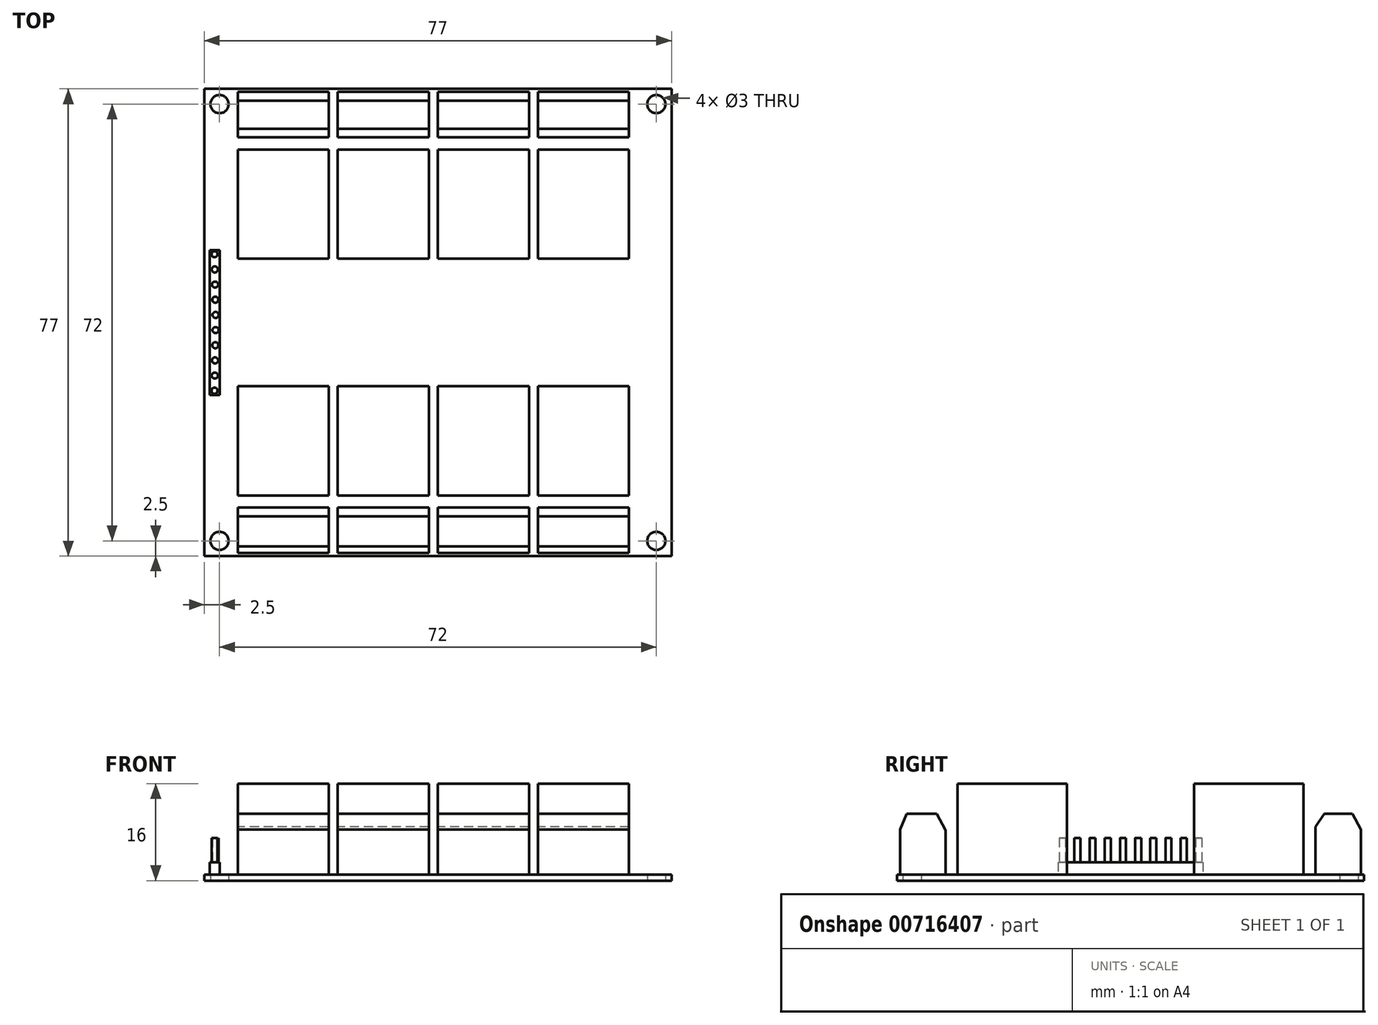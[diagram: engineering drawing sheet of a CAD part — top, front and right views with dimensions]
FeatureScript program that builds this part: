
annotation { "Feature Type Name" : "Feature", "Feature Type Description" : "" }
export const myFeature = defineFeature(function(context is Context, id is Id, definition is map)
    precondition{}
    {
        {
            var Q0;
            Q0=qCreatedBy(makeId("Top.planeOp"),FACE);
            var sketch = newSketch(context, id + "F0", { "sketchPlane" : qUnion([Q0])});
            skLineSegment(sketch, "E0.bottom", {"start": v(0, 0) * mm, "end": v(77, 0) * mm});
            skLineSegment(sketch, "E0.top", {"start": v(0, 77) * mm, "end": v(77, 77) * mm});
            skLineSegment(sketch, "E0.left", {"start": v(0, 0) * mm, "end": v(0, 77) * mm});
            skLineSegment(sketch, "E0.right", {"start": v(77, 0) * mm, "end": v(77, 77) * mm});
            skLineSegment(sketch, "E1", {"start": v(38.5, 77) * mm, "end": v(38.5, 0) * mm, "construction": true});
            skLineSegment(sketch, "E2", {"start": v(77, 38.5) * mm, "end": v(0, 38.5) * mm, "construction": true});
            skCircle(sketch, "E3", {"center": v(2.5, 2.5) * mm, "radius": 1.5 * mm});
            skCircle(sketch, "E4.MirrorC", {"center": v(74.5, 2.5) * mm, "radius": 1.5 * mm});
            skLineSegment(sketch, "E5.MirrorCS", {"start": v(0, 38.5) * mm, "end": v(77, 38.5) * mm, "construction": true});
            skCircle(sketch, "E6.MirrorC", {"center": v(74.5, 74.5) * mm, "radius": 1.5 * mm});
            skCircle(sketch, "E7.MirrorC", {"center": v(2.5, 74.5) * mm, "radius": 1.5 * mm});
            skSolve(sketch);
        }
        {
            var Q0;
            Q0 = qSketchRegion(id + "F0", true);
            extrude(context, id + "F1", {"entities" : qUnion([Q0]), "depth" : 1 * mm, "offsetDistance" : 25 * mm});
        }
        {
            var Q0;
            Q0=makeQuery(id+"F1.opExtrude","CAP_FACE",FACE,{"disambiguationData":[OSD([sQuery(id+"F0.wireOp",EDGE,"E0.bottom"),sQuery(id+"F0.wireOp",EDGE,"E0.top"),sQuery(id+"F0.wireOp",EDGE,"E0.left"),sQuery(id+"F0.wireOp",EDGE,"E0.right"),sQuery(id+"F0.wireOp",EDGE,"E3"),sQuery(id+"F0.wireOp",EDGE,"E4.MirrorC"),sQuery(id+"F0.wireOp",EDGE,"E6.MirrorC"),sQuery(id+"F0.wireOp",EDGE,"E7.MirrorC")])],"isStart":false});
            var sketch = newSketch(context, id + "F2", { "sketchPlane" : qUnion([Q0])});
            skLineSegment(sketch, "E8.bottom", {"start": v(5.5, 67) * mm, "end": v(20.5, 67) * mm});
            skLineSegment(sketch, "E8.top", {"start": v(5.5, 49) * mm, "end": v(20.5, 49) * mm});
            skLineSegment(sketch, "E8.left", {"start": v(5.5, 67) * mm, "end": v(5.5, 49) * mm});
            skLineSegment(sketch, "E8.right", {"start": v(20.5, 67) * mm, "end": v(20.5, 49) * mm});
            skLineSegment(sketch, "E9.1.0.0", {"start": v(37, 67) * mm, "end": v(37, 49) * mm});
            skLineSegment(sketch, "E9.1.0.1", {"start": v(22, 67) * mm, "end": v(22, 49) * mm});
            skLineSegment(sketch, "E9.1.0.2", {"start": v(22, 49) * mm, "end": v(37, 49) * mm});
            skLineSegment(sketch, "E9.1.0.3", {"start": v(22, 67) * mm, "end": v(37, 67) * mm});
            skLineSegment(sketch, "E9.2.0.0", {"start": v(53.5, 67) * mm, "end": v(53.5, 49) * mm});
            skLineSegment(sketch, "E9.2.0.1", {"start": v(38.5, 67) * mm, "end": v(38.5, 49) * mm});
            skLineSegment(sketch, "E9.2.0.2", {"start": v(38.5, 49) * mm, "end": v(53.5, 49) * mm});
            skLineSegment(sketch, "E9.2.0.3", {"start": v(38.5, 67) * mm, "end": v(53.5, 67) * mm});
            skLineSegment(sketch, "E9.3.0.0", {"start": v(70, 67) * mm, "end": v(70, 49) * mm});
            skLineSegment(sketch, "E9.3.0.1", {"start": v(55, 67) * mm, "end": v(55, 49) * mm});
            skLineSegment(sketch, "E9.3.0.2", {"start": v(55, 49) * mm, "end": v(70, 49) * mm});
            skLineSegment(sketch, "E9.3.0.3", {"start": v(55, 67) * mm, "end": v(70, 67) * mm});
            skLineSegment(sketch, "E9.direction1", {"start": v(5.5, 49) * mm, "end": v(22, 49) * mm, "construction": true});
            skLineSegment(sketch, "E10", {"start": v(0, 38.5) * mm, "end": v(77, 38.5) * mm, "construction": true});
            skLineSegment(sketch, "E11.MirrorCS", {"start": v(5.5, 28) * mm, "end": v(20.5, 28) * mm});
            skLineSegment(sketch, "E12.MirrorCS", {"start": v(22, 10) * mm, "end": v(37, 10) * mm});
            skLineSegment(sketch, "E13.MirrorCS", {"start": v(53.5, 10) * mm, "end": v(53.5, 28) * mm});
            skLineSegment(sketch, "E14.MirrorCS", {"start": v(22, 28) * mm, "end": v(37, 28) * mm});
            skLineSegment(sketch, "E15.MirrorCS", {"start": v(22, 10) * mm, "end": v(22, 28) * mm});
            skLineSegment(sketch, "E16.MirrorCS", {"start": v(37, 10) * mm, "end": v(37, 28) * mm});
            skLineSegment(sketch, "E17.MirrorCS", {"start": v(20.5, 10) * mm, "end": v(20.5, 28) * mm});
            skLineSegment(sketch, "E18.MirrorCS", {"start": v(5.5, 10) * mm, "end": v(5.5, 28) * mm});
            skLineSegment(sketch, "E19.MirrorCS", {"start": v(5.5, 10) * mm, "end": v(20.5, 10) * mm});
            skLineSegment(sketch, "E20.MirrorCS", {"start": v(55, 10) * mm, "end": v(70, 10) * mm});
            skLineSegment(sketch, "E21.MirrorCS", {"start": v(55, 28) * mm, "end": v(70, 28) * mm});
            skLineSegment(sketch, "E22.MirrorCS", {"start": v(55, 10) * mm, "end": v(55, 28) * mm});
            skLineSegment(sketch, "E23.MirrorCS", {"start": v(5.5, 28) * mm, "end": v(22, 28) * mm, "construction": true});
            skLineSegment(sketch, "E24.MirrorCS", {"start": v(38.5, 10) * mm, "end": v(38.5, 28) * mm});
            skLineSegment(sketch, "E25.MirrorCS", {"start": v(38.5, 28) * mm, "end": v(53.5, 28) * mm});
            skLineSegment(sketch, "E26.MirrorCS", {"start": v(38.5, 10) * mm, "end": v(53.5, 10) * mm});
            skLineSegment(sketch, "E27.MirrorCS", {"start": v(70, 10) * mm, "end": v(70, 28) * mm});
            skSolve(sketch);
        }
        {
            var Q0;
            Q0 = qSketchRegion(id + "F2", true);
            extrude(context, id + "F3", {"entities" : qUnion([Q0]), "operationType" : NewBodyOperationType.ADD, "depth" : 15 * mm, "offsetDistance" : 25 * mm});
        }
        {
            var Q0;
            Q0=makeQuery(id+"F1.opExtrude","CAP_FACE",FACE,{"disambiguationData":[OSD([sQuery(id+"F0.wireOp",EDGE,"E0.bottom"),sQuery(id+"F0.wireOp",EDGE,"E0.top"),sQuery(id+"F0.wireOp",EDGE,"E0.left"),sQuery(id+"F0.wireOp",EDGE,"E0.right"),sQuery(id+"F0.wireOp",EDGE,"E3"),sQuery(id+"F0.wireOp",EDGE,"E4.MirrorC"),sQuery(id+"F0.wireOp",EDGE,"E6.MirrorC"),sQuery(id+"F0.wireOp",EDGE,"E7.MirrorC")])],"isStart":false});
            var sketch = newSketch(context, id + "F4", { "sketchPlane" : qUnion([Q0])});
            skLineSegment(sketch, "E28.bottom", {"start": v(5.5, 69) * mm, "end": v(20.5, 69) * mm});
            skLineSegment(sketch, "E28.top", {"start": v(5.5, 76.5) * mm, "end": v(20.5, 76.5) * mm});
            skLineSegment(sketch, "E28.left", {"start": v(5.5, 69) * mm, "end": v(5.5, 76.5) * mm});
            skLineSegment(sketch, "E28.right", {"start": v(20.5, 69) * mm, "end": v(20.5, 76.5) * mm});
            skLineSegment(sketch, "E29.1.0.0", {"start": v(37, 69) * mm, "end": v(37, 76.5) * mm});
            skLineSegment(sketch, "E29.1.0.1", {"start": v(22, 69) * mm, "end": v(22, 76.5) * mm});
            skLineSegment(sketch, "E29.1.0.2", {"start": v(22, 76.5) * mm, "end": v(37, 76.5) * mm});
            skLineSegment(sketch, "E29.1.0.3", {"start": v(22, 69) * mm, "end": v(37, 69) * mm});
            skLineSegment(sketch, "E29.2.0.0", {"start": v(53.5, 69) * mm, "end": v(53.5, 76.5) * mm});
            skLineSegment(sketch, "E29.2.0.1", {"start": v(38.5, 69) * mm, "end": v(38.5, 76.5) * mm});
            skLineSegment(sketch, "E29.2.0.2", {"start": v(38.5, 76.5) * mm, "end": v(53.5, 76.5) * mm});
            skLineSegment(sketch, "E29.2.0.3", {"start": v(38.5, 69) * mm, "end": v(53.5, 69) * mm});
            skLineSegment(sketch, "E29.3.0.0", {"start": v(70, 69) * mm, "end": v(70, 76.5) * mm});
            skLineSegment(sketch, "E29.3.0.1", {"start": v(55, 69) * mm, "end": v(55, 76.5) * mm});
            skLineSegment(sketch, "E29.3.0.2", {"start": v(55, 76.5) * mm, "end": v(70, 76.5) * mm});
            skLineSegment(sketch, "E29.3.0.3", {"start": v(55, 69) * mm, "end": v(70, 69) * mm});
            skLineSegment(sketch, "E30", {"start": v(0, 38.5) * mm, "end": v(77, 38.5) * mm, "construction": true});
            skLineSegment(sketch, "E31.MirrorCS", {"start": v(55, 8) * mm, "end": v(55, 0.5) * mm});
            skLineSegment(sketch, "E32.MirrorCS", {"start": v(55, 0.5) * mm, "end": v(70, 0.5) * mm});
            skLineSegment(sketch, "E33.MirrorCS", {"start": v(55, 8) * mm, "end": v(70, 8) * mm});
            skLineSegment(sketch, "E34.MirrorCS", {"start": v(5.5, 8) * mm, "end": v(20.5, 8) * mm});
            skLineSegment(sketch, "E35.MirrorCS", {"start": v(22, 8) * mm, "end": v(22, 0.5) * mm});
            skLineSegment(sketch, "E36.MirrorCS", {"start": v(70, 8) * mm, "end": v(70, 0.5) * mm});
            skLineSegment(sketch, "E37.MirrorCS", {"start": v(5.5, 0.5) * mm, "end": v(20.5, 0.5) * mm});
            skLineSegment(sketch, "E38.MirrorCS", {"start": v(20.5, 8) * mm, "end": v(20.5, 0.5) * mm});
            skLineSegment(sketch, "E39.MirrorCS", {"start": v(37, 8) * mm, "end": v(37, 0.5) * mm});
            skLineSegment(sketch, "E40.MirrorCS", {"start": v(38.5, 8) * mm, "end": v(38.5, 0.5) * mm});
            skLineSegment(sketch, "E41.MirrorCS", {"start": v(5.5, 8) * mm, "end": v(5.5, 0.5) * mm});
            skLineSegment(sketch, "E42.MirrorCS", {"start": v(22, 8) * mm, "end": v(37, 8) * mm});
            skLineSegment(sketch, "E43.MirrorCS", {"start": v(38.5, 8) * mm, "end": v(53.5, 8) * mm});
            skLineSegment(sketch, "E44.MirrorCS", {"start": v(38.5, 0.5) * mm, "end": v(53.5, 0.5) * mm});
            skLineSegment(sketch, "E45.MirrorCS", {"start": v(53.5, 8) * mm, "end": v(53.5, 0.5) * mm});
            skLineSegment(sketch, "E46.MirrorCS", {"start": v(22, 0.5) * mm, "end": v(37, 0.5) * mm});
            skSolve(sketch);
        }
        {
            var Q0;
            Q0 = qSketchRegion(id + "F4", true);
            extrude(context, id + "F5", {"entities" : qUnion([Q0]), "operationType" : NewBodyOperationType.ADD, "depth" : 10 * mm, "offsetDistance" : 25 * mm});
        }
        {
            var Q0;
            Q0=makeQuery(id+"F1.opExtrude","CAP_FACE",FACE,{"disambiguationData":[OSD([sQuery(id+"F0.wireOp",EDGE,"E0.bottom"),sQuery(id+"F0.wireOp",EDGE,"E0.top"),sQuery(id+"F0.wireOp",EDGE,"E0.left"),sQuery(id+"F0.wireOp",EDGE,"E0.right"),sQuery(id+"F0.wireOp",EDGE,"E3"),sQuery(id+"F0.wireOp",EDGE,"E4.MirrorC"),sQuery(id+"F0.wireOp",EDGE,"E6.MirrorC"),sQuery(id+"F0.wireOp",EDGE,"E7.MirrorC")])],"isStart":false});
            var sketch = newSketch(context, id + "F6", { "sketchPlane" : qUnion([Q0])});
            skLineSegment(sketch, "E47", {"start": v(0, 38.5) * mm, "end": v(77, 38.5) * mm, "construction": true});
            skCircle(sketch, "E48", {"center": v(1.86, 39.75) * mm, "radius": 0.5 * mm});
            skCircle(sketch, "E49.1.0.0", {"center": v(1.81, 42.25) * mm, "radius": 0.5 * mm});
            skCircle(sketch, "E49.2.0.0", {"center": v(1.77, 44.75) * mm, "radius": 0.5 * mm});
            skCircle(sketch, "E49.3.0.0", {"center": v(1.73, 47.25) * mm, "radius": 0.5 * mm});
            skCircle(sketch, "E49.4.0.0", {"center": v(1.68, 49.75) * mm, "radius": 0.5 * mm});
            skCircle(sketch, "E50.MirrorC", {"center": v(1.86, 37.25) * mm, "radius": 0.5 * mm});
            skCircle(sketch, "E51.MirrorC", {"center": v(1.77, 32.25) * mm, "radius": 0.5 * mm});
            skCircle(sketch, "E52.MirrorC", {"center": v(1.68, 27.25) * mm, "radius": 0.5 * mm});
            skCircle(sketch, "E53.MirrorC", {"center": v(1.73, 29.75) * mm, "radius": 0.5 * mm});
            skCircle(sketch, "E54.MirrorC", {"center": v(1.81, 34.75) * mm, "radius": 0.5 * mm});
            skSolve(sketch);
        }
        {
            var Q0;
            Q0 = qSketchRegion(id + "F6", true);
            extrude(context, id + "F7", {"entities" : qUnion([Q0]), "operationType" : NewBodyOperationType.ADD, "depth" : 6 * mm, "offsetDistance" : 25 * mm});
        }
        {
            var Q0;
            Q0=makeQuery(id+"F5.opExtrude","SWEPT_FACE",FACE,{"disambiguationData":[OSD([sQuery(id+"F4.wireOp",EDGE,"E28.left")])]});
            var sketch = newSketch(context, id + "F8", { "sketchPlane" : qUnion([Q0])});
            skLineSegment(sketch, "E55", {"start": v(-75.06, 11) * mm, "end": v(-76.5, 8.45) * mm});
            skLineSegment(sketch, "E56", {"start": v(-76.5, 8.45) * mm, "end": v(-76.5, 11) * mm});
            skLineSegment(sketch, "E57", {"start": v(-76.5, 11) * mm, "end": v(-75.06, 11) * mm});
            skLineSegment(sketch, "E58", {"start": v(-69, 11) * mm, "end": v(-70.42, 11) * mm});
            skLineSegment(sketch, "E59", {"start": v(-70.42, 11) * mm, "end": v(-69, 8.88) * mm});
            skLineSegment(sketch, "E60", {"start": v(-69, 8.88) * mm, "end": v(-69, 11) * mm});
            skLineSegment(sketch, "E61", {"start": v(-8.03, 11) * mm, "end": v(-8.03, 8.25) * mm});
            skLineSegment(sketch, "E62", {"start": v(-8.03, 8.25) * mm, "end": v(-6.55, 11) * mm});
            skLineSegment(sketch, "E63", {"start": v(-6.55, 11) * mm, "end": v(-8.03, 11) * mm});
            skLineSegment(sketch, "E64", {"start": v(-0.5, 11) * mm, "end": v(-0.5, 8.42) * mm});
            skLineSegment(sketch, "E65", {"start": v(-0.5, 8.42) * mm, "end": v(-1.62, 11) * mm});
            skLineSegment(sketch, "E66", {"start": v(-1.62, 11) * mm, "end": v(-0.5, 11) * mm});
            skSolve(sketch);
        }
        {
            var Q0;
            Q0 = qSketchRegion(id + "F8", true);
            extrude(context, id + "F9", {"entities" : qUnion([Q0]), "operationType" : NewBodyOperationType.REMOVE, "endBound" : BoundingType.THROUGH_ALL, "oppositeDirection" : true, "depth" : 25 * mm, "offsetDistance" : 25 * mm});
        }
        {
            var Q0;
            Q0=makeQuery(id+"F1.opExtrude","CAP_FACE",FACE,{"disambiguationData":[OSD([sQuery(id+"F0.wireOp",EDGE,"E0.bottom"),sQuery(id+"F0.wireOp",EDGE,"E0.top"),sQuery(id+"F0.wireOp",EDGE,"E0.left"),sQuery(id+"F0.wireOp",EDGE,"E0.right"),sQuery(id+"F0.wireOp",EDGE,"E3"),sQuery(id+"F0.wireOp",EDGE,"E4.MirrorC"),sQuery(id+"F0.wireOp",EDGE,"E6.MirrorC"),sQuery(id+"F0.wireOp",EDGE,"E7.MirrorC")])],"isStart":false});
            var sketch = newSketch(context, id + "F10", { "sketchPlane" : qUnion([Q0])});
            skLineSegment(sketch, "E67.bottom", {"start": v(0.91, 26.57) * mm, "end": v(2.57, 26.57) * mm});
            skLineSegment(sketch, "E67.top", {"start": v(0.91, 50.43) * mm, "end": v(2.57, 50.43) * mm});
            skLineSegment(sketch, "E67.left", {"start": v(0.91, 26.57) * mm, "end": v(0.91, 50.43) * mm});
            skLineSegment(sketch, "E67.right", {"start": v(2.57, 26.57) * mm, "end": v(2.57, 50.43) * mm});
            skPoint(sketch, "E67.middle", {"position": v(1.74, 38.5) * mm});
            skPoint(sketch, "E67.middle.positionSnap0", {"position": v(0, 38.5) * mm});
            skPoint(sketch, "E67.centerSnap0", {"position": v(0, 38.5) * mm});
            skSolve(sketch);
        }
        {
            var Q0;
            Q0 = qSketchRegion(id + "F10", true);
            extrude(context, id + "F11", {"entities" : qUnion([Q0]), "operationType" : NewBodyOperationType.ADD, "depth" : 2 * mm, "offsetDistance" : 25 * mm});
        }
    });
